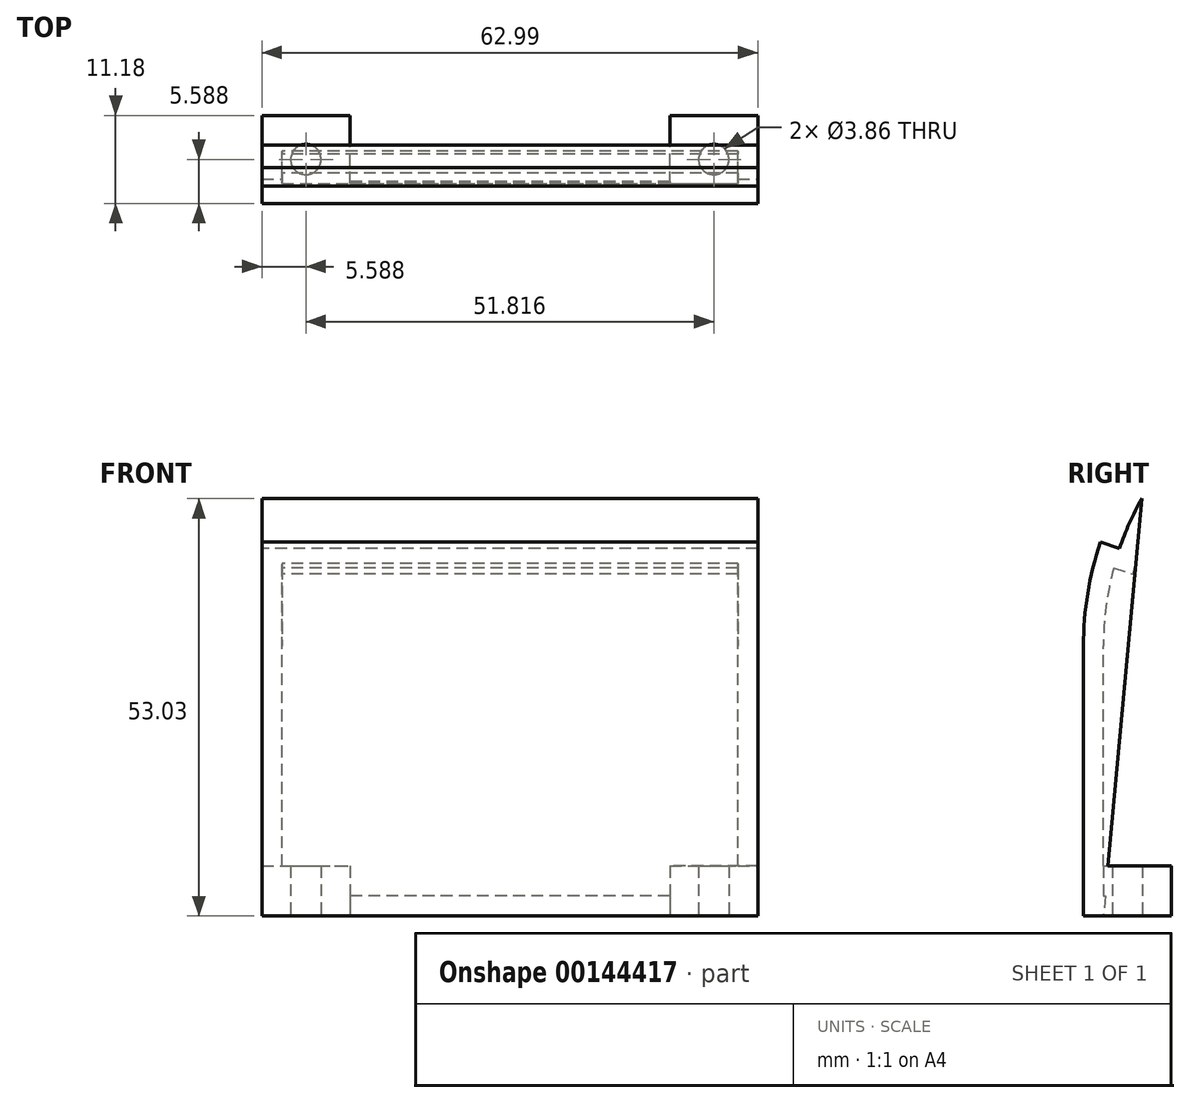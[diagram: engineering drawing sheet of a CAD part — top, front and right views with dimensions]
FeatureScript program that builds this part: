
annotation { "Feature Type Name" : "Feature", "Feature Type Description" : "" }
export const myFeature = defineFeature(function(context is Context, id is Id, definition is map)
    precondition{}
    {
        {
            var Q0;
            Q0=qCreatedBy(makeId("Right.planeOp"),FACE);
            var sketch = newSketch(context, id + "F0", { "sketchPlane" : qUnion([Q0])});
            skLineSegment(sketch, "E0", {"start": v(0, 0) * mm, "end": v(0, 34.3) * mm});
            skLineSegment(sketch, "E1", {"start": v(0, 34.3) * mm, "end": v(2.54, 34.3) * mm, "construction": true});
            skLineSegment(sketch, "E2", {"start": v(2.54, 34.3) * mm, "end": v(2.54, 0) * mm});
            skLineSegment(sketch, "E3", {"start": v(2.54, 0) * mm, "end": v(0, 0) * mm});
            skArc(sketch, "E4", {"start": v(2.18, 47.5) * mm, "mid": v(0.55, 40.98) * mm, "end": v(0, 34.3) * mm});
            skArc(sketch, "E5.0", {"start": v(7.4, 53.03) * mm, "mid": v(3.77, 43.97) * mm, "end": v(2.54, 34.3) * mm});
            skLineSegment(sketch, "E6", {"start": v(2.18, 47.5) * mm, "end": v(4.58, 46.68) * mm});
            skLineSegment(sketch, "E7", {"start": v(2.18, 47.5) * mm, "end": v(4.22, 53.51) * mm, "construction": true});
            skLineSegment(sketch, "E8", {"start": v(2.54, 0) * mm, "end": v(7.4, 53.03) * mm});
            skSolve(sketch);
        }
        {
            var Q0;
            Q0=makeQuery(id+"F0.imprint","IMPRINT",FACE,{"disambiguationData":[TD([[makeQuery(id+"F0.imprint","IMPRINT",EDGE,{"derivedFrom":sQuery(id+"F0.wireOp",EDGE,"E0")}),-1.0]])]});
            var Q1;
            {var subQ0=sQuery(id+"F0.wireOp",EDGE,"E2");Q1=makeQuery(id+"F0.imprint","IMPRINT",FACE,{"disambiguationData":[TD([[makeQuery(id+"F0.imprint","IMPRINT",EDGE,{"derivedFrom":subQ0}),1.0]])]});}
            extrude(context, id + "F1", {"entities" : qUnion([Q0, Q1]), "depth" : 63 * mm});
        }
        {
            var Q0;
            Q0=makeQuery(id+"F1.opExtrude","SWEPT_FACE",FACE,{"disambiguationData":[OSD([sQuery(id+"F0.wireOp",EDGE,"E8")])]});
            shell(context, id + "F2", {"entities" : qUnion([Q0]), "thickness" : 2.54 * mm});
        }
        {
            var Q0;
            Q0=makeQuery(id+"F1.opExtrude","SWEPT_FACE",FACE,{"disambiguationData":[OSD([sQuery(id+"F0.wireOp",EDGE,"E3")])]});
            var sketch = newSketch(context, id + "F3", { "sketchPlane" : qUnion([Q0])});
            skLineSegment(sketch, "E9.bottom", {"start": v(63, 0) * mm, "end": v(51.82, 0) * mm});
            skLineSegment(sketch, "E9.top", {"start": v(63, -11.18) * mm, "end": v(51.82, -11.18) * mm});
            skLineSegment(sketch, "E9.left", {"start": v(63, 0) * mm, "end": v(63, -11.18) * mm});
            skLineSegment(sketch, "E9.right", {"start": v(51.82, 0) * mm, "end": v(51.82, -11.18) * mm});
            skLineSegment(sketch, "E10.bottom", {"start": v(0, 0) * mm, "end": v(11.18, 0) * mm});
            skLineSegment(sketch, "E10.top", {"start": v(0, -11.18) * mm, "end": v(11.18, -11.18) * mm});
            skLineSegment(sketch, "E10.left", {"start": v(0, 0) * mm, "end": v(0, -11.18) * mm});
            skLineSegment(sketch, "E10.right", {"start": v(11.18, 0) * mm, "end": v(11.18, -11.18) * mm});
            skLineSegment(sketch, "E11", {"start": v(63, -11.18) * mm, "end": v(51.82, 0) * mm, "construction": true});
            skLineSegment(sketch, "E12", {"start": v(11.18, 0) * mm, "end": v(0, -11.18) * mm, "construction": true});
            skCircle(sketch, "E13", {"center": v(57.4, -5.59) * mm, "radius": 1.93 * mm});
            skCircle(sketch, "E14", {"center": v(5.59, -5.59) * mm, "radius": 1.93 * mm});
            skSolve(sketch);
        }
        {
            var Q0;
            Q0 = qSketchRegion(id + "F3", true);
            extrude(context, id + "F4", {"entities" : qUnion([Q0]), "operationType" : NewBodyOperationType.ADD, "oppositeDirection" : true, "depth" : 6.35 * mm});
        }
    });
